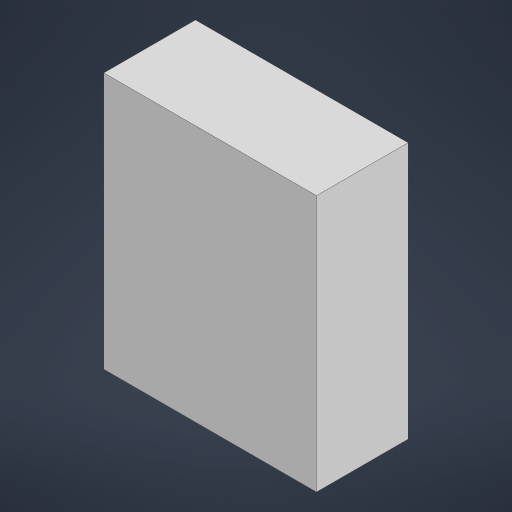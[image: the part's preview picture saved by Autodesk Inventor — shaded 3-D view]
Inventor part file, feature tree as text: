
AUTODESK INVENTOR PART (.ipt)
format: ipt  version: 2023 (Build 270158000, 158)  size: 140,800 bytes
history: native  units: in
note: dims shown in document units (in); Inventor stores cm internally (conversion verified against a paired STEP export)
features: extrude x1, sketch x1
ambient origin geometry x8: Origin, YZ Plane, XZ Plane, XY Plane, X Axis, Y Axis, Z Axis, Center Point
bodies: Solid1 (feature_tree)
feature tree (2):
  extrude  "Extrusion1"  Depth=0.1378in
  sketch  "Sketch1"  dims[d0=0.1142in d1=0.1378in d2=0.0492in d3=0.0in]
